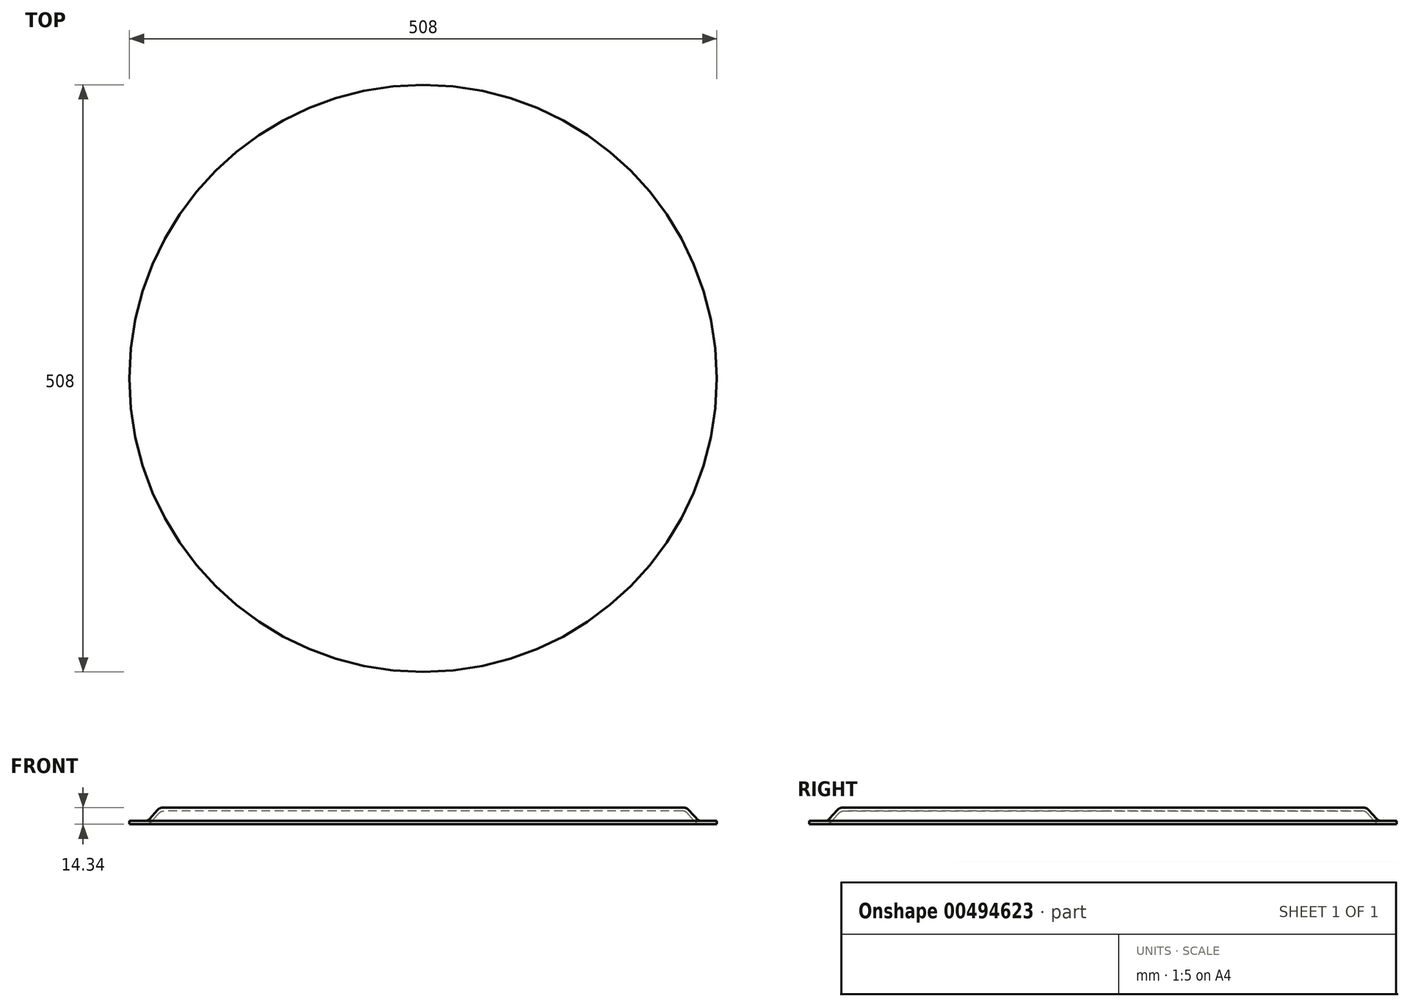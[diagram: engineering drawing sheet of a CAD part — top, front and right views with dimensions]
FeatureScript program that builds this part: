
annotation { "Feature Type Name" : "Feature", "Feature Type Description" : "" }
export const myFeature = defineFeature(function(context is Context, id is Id, definition is map)
    precondition{}
    {
        {
            var Q0;
            Q0=qCreatedBy(makeId("Front.planeOp"),FACE);
            var sketch = newSketch(context, id + "F0", { "sketchPlane" : qUnion([Q0])});
            skLineSegment(sketch, "E0", {"start": v(0, 0) * mm, "end": v(225.45, 0) * mm});
            skLineSegment(sketch, "E1", {"start": v(229.61, -1.84) * mm, "end": v(236.77, -9.69) * mm});
            skLineSegment(sketch, "E2", {"start": v(240.94, -11.52) * mm, "end": v(254, -11.52) * mm});
            skLineSegment(sketch, "E3.0", {"start": v(239.7, -14.34) * mm, "end": v(254, -14.34) * mm});
            skLineSegment(sketch, "E3.1", {"start": v(228.37, -4.65) * mm, "end": v(235.53, -12.5) * mm});
            skLineSegment(sketch, "E3.2", {"start": v(0, -2.82) * mm, "end": v(224.2, -2.82) * mm});
            skLineSegment(sketch, "E4", {"start": v(0, 0) * mm, "end": v(0, -2.82) * mm});
            skLineSegment(sketch, "E5", {"start": v(254, -11.52) * mm, "end": v(254, -14.34) * mm});
            skPoint(sketch, "E6.visualSharp", {"position": v(227.93, 0) * mm});
            skArc(sketch, "E6.filletArc", {"start": v(229.61, -1.84) * mm, "mid": v(227.72, -0.48) * mm, "end": v(225.45, 0) * mm});
            skPoint(sketch, "E7.visualSharp", {"position": v(226.7, -2.82) * mm});
            skArc(sketch, "E7.filletArc", {"start": v(228.37, -4.65) * mm, "mid": v(226.48, -3.3) * mm, "end": v(224.2, -2.82) * mm});
            skPoint(sketch, "E8.visualSharp", {"position": v(238.45, -11.52) * mm});
            skArc(sketch, "E8.filletArc", {"start": v(236.77, -9.69) * mm, "mid": v(238.66, -11.04) * mm, "end": v(240.94, -11.52) * mm});
            skPoint(sketch, "E9.visualSharp", {"position": v(237.2, -14.34) * mm});
            skArc(sketch, "E9.filletArc", {"start": v(235.53, -12.5) * mm, "mid": v(237.42, -13.86) * mm, "end": v(239.7, -14.34) * mm});
            skSolve(sketch);
        }
        {
            var Q0;
            Q0=makeQuery(id+"F0.imprint","IMPRINT",FACE,{"disambiguationData":[TD([[makeQuery(id+"F0.imprint","IMPRINT",EDGE,{"derivedFrom":sQuery(id+"F0.wireOp",EDGE,"E0")}),-1.0]])]});
            var Q1;
            Q1=sQuery(id+"F0.wireOp",EDGE,"E4");
            revolve(context, id + "F1", {"entities" : qUnion([Q0]), "axis" : qUnion([Q1]), "revolveType" : RevolveType.FULL});
        }
    });
